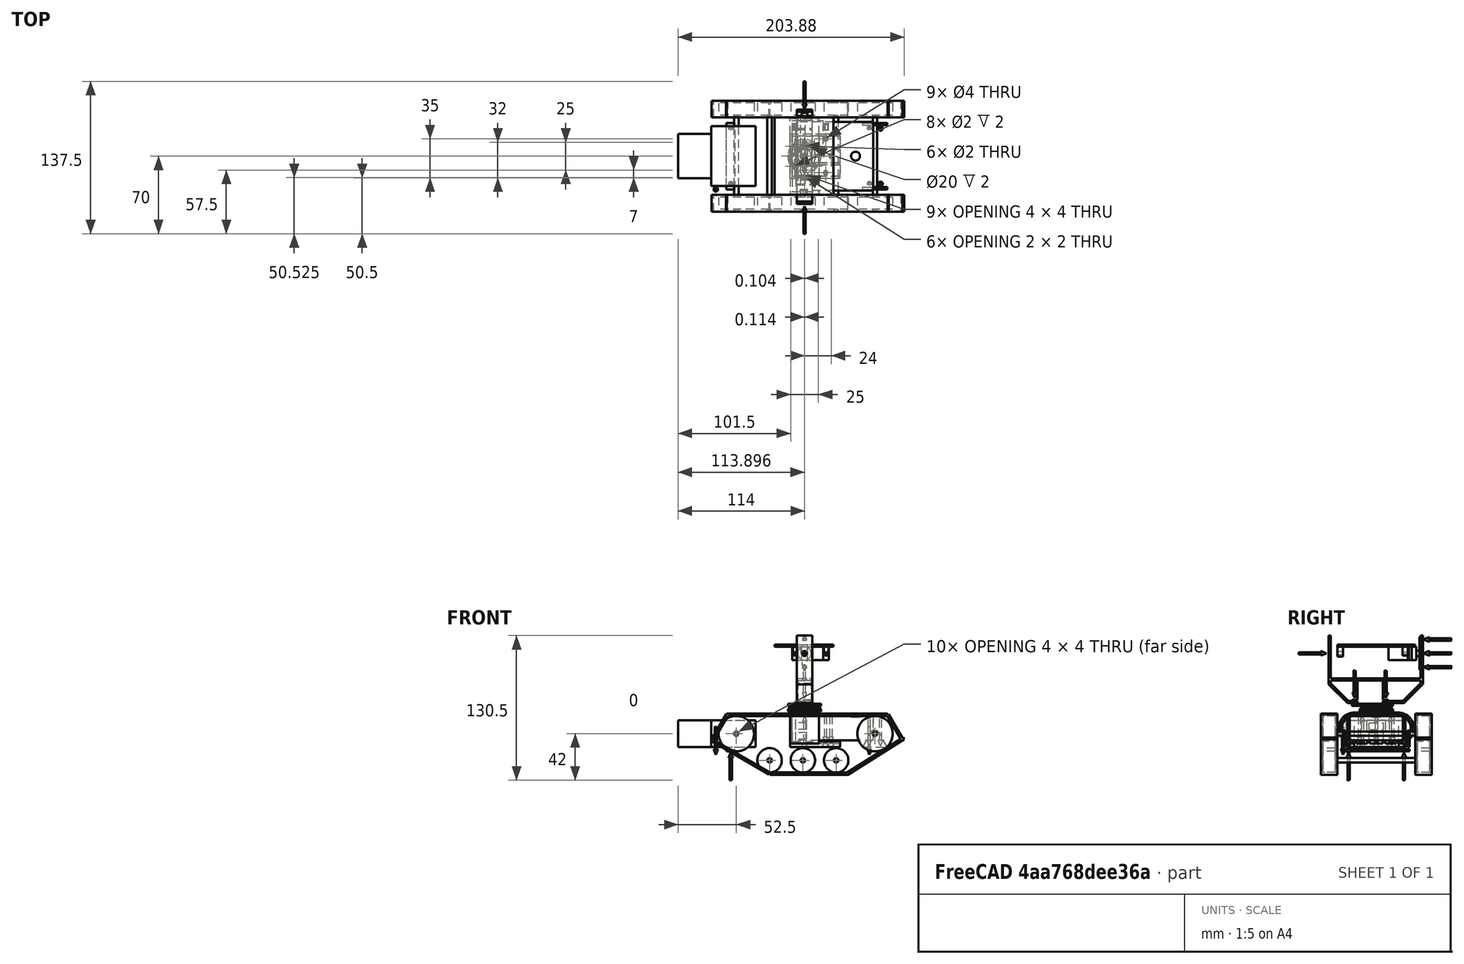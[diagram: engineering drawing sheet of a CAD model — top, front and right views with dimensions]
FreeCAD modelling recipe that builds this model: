
FCSTD DOCUMENT
Label: androidtank_9
License: CC-BY 3.0
LicenseURL: http://creativecommons.org/licenses/by/3.0/
objects: Part::Cylinder×57, Part::MultiFuse×45, Part::Box×39, Part::Cut×9, Part::Sphere×8, App::DocumentObjectGroup×2, Part::FeaturePython×1, Mesh::Feature×1, Part::Cone×1
note: 160 computed .brp shape members not serialized (recipe doc carries the construction recipe); baked Part::Feature solids carry a one-line shape summary decoded from their .brp

FEATURE [Part::Box] Box001001  label="Moter Unit2"
  Height = 24
  Length = 30
  Placement = pos=(-34,10,2) rot=(0,0,1;0rad)
  Width = 40
FEATURE [Part::Cylinder] Cylinder  label="Shaft"
  Angle = 360
  Height = 100
  Placement = pos=(20,-20,14) rot=(-1,0,0;1.5708rad)
  Radius = 2
FEATURE [Part::Box] Box001002
  Height = 2
  Length = 145
  Placement = pos=(10,-20,30) rot=(0,0,1;0rad)
  Width = 15
FEATURE [Part::Box] Box001002001
  Height = 2
  Length = 70
  Placement = pos=(49,-20,-23) rot=(0,0,1;0rad)
  Width = 15
FEATURE [Part::Box] Box001002001001
  Height = 2
  Length = 60
  Placement = pos=(119,-20,-23) rot=(0,-1,0;0.558505rad)
  Width = 15
FEATURE [Part::Box] Box001002001002
  Height = 2
  Length = 60
  Placement = pos=(49,-20,-21) rot=(0,1,0;3.66519rad)
  Width = 15
FEATURE [Part::Box] Box001002001003
  Height = 2
  Length = 26
  Placement = pos=(-2,-20,8) rot=(0,-1,0;1.0472rad)
  Width = 15
FEATURE [Part::Box] Box001002001003001
  Height = 2
  Length = 26
  Placement = pos=(169,-20,9) rot=(0,-1,0;2.0944rad)
  Width = 15
FEATURE [Part::MultiFuse] Fusion002001002  label="Caterpiller1"
  Shapes = -> [Box001002,Box001002001,Box001002001002,Box001002001001,Box001002001003,Box001002001003001]
FEATURE [Part::MultiFuse] Fusion002001002001  label="Caterpiller2"
  Placement = pos=(0,85,0) rot=(0,0,1;0rad)
  Shapes = -> [Box001002,Box001002001,Box001002001002,Box001002001001,Box001002001003,Box001002001003001]
FEATURE [Part::Cylinder] Cylinder002001001002  label="Wheel006"
  Angle = 360
  Height = 11
  Placement = pos=(20,78,14) rot=(1,0,0;1.5708rad)
  Radius = 11
FEATURE [Part::Cylinder] Cylinder002001001002001  label="Wheel007"
  Angle = 360
  Height = 11
  Placement = pos=(20,-7,14) rot=(1,0,0;1.5708rad)
  Radius = 11
FEATURE [Part::Cylinder] Cylinder002001002001  label="Shaft002"
  Angle = 360
  Height = 100
  Placement = pos=(20,-20,14) rot=(-1,0,0;1.5708rad)
  Radius = 2
FEATURE [Part::MultiFuse] Fusion002001002002002  label="SWheelSet1"
  Placement = pos=(28.5,0,-24) rot=(0,0,1;0rad)
  Shapes = -> [Cylinder002001002001,Cylinder002001001002,Cylinder002001001002001]
FEATURE [Part::MultiFuse] Fusion002001002002002001  label="SWheelSet2"
  Placement = pos=(58.5,0,-24) rot=(0,0,1;0rad)
  Shapes = -> [Cylinder002001002001,Cylinder002001001002,Cylinder002001001002001]
FEATURE [Part::MultiFuse] Fusion002001002002002001001  label="SWheelSet3"
  Placement = pos=(88.5,0,-24) rot=(0,0,1;0rad)
  Shapes = -> [Cylinder002001002001,Cylinder002001001002,Cylinder002001001002001]
FEATURE [Part::Box] Box001002001003002
  Height = 22
  Length = 70
  Placement = pos=(0,0,-11) rot=(0,0,1;0rad)
  Width = 40
FEATURE [Part::Cylinder] Cylinder002001001002002
  Angle = 360
  Height = 70
  Placement = pos=(0,0,0) rot=(0,1,0;1.5708rad)
  Radius = 11
FEATURE [Part::Cylinder] Cylinder001
  Angle = 360
  Height = 70
  Placement = pos=(0,40,0) rot=(0,1,0;1.5708rad)
  Radius = 11
FEATURE [Part::Cylinder] Cylinder002001001002003  label="PowerButton"
  Angle = 360
  Height = 2
  Placement = pos=(16,20,10) rot=(0,0,1;0rad)
  Radius = 4
FEATURE [Part::Box] Box001002001003003  label="USB1"
  Height = 6
  Length = 15
  Placement = pos=(60,13.5,-1) rot=(0,0,1;0rad)
  Width = 13
FEATURE [Part::Box] Box001001001  label="USB2"
  Height = 6
  Length = 15
  Placement = pos=(60,13.5,-10) rot=(0,0,1;0rad)
  Width = 13
FEATURE [Part::MultiFuse] Fusion002001002002002001002
  Shapes = -> [Cylinder001,Box001002001003002,Cylinder002001001002002]
FEATURE [Part::MultiFuse] Fusion001001
  Shapes = -> [Box001001001,Cylinder002001001002003,Box001002001003003]
FEATURE [Part::Cut] Cut  label="Eneloop"
  Base = -> Fusion002001002002002001002
  Placement = pos=(142,50,19) rot=(0,0,1;3.14159rad)
  Tool = -> Fusion001001
FEATURE [Part::Cylinder] Cylinder001001  label="Cylinder002"
  Angle = 360
  Height = 26
  Placement = pos=(0,50,19) rot=(0,1,0;1.5708rad)
  Radius = 14
FEATURE [Part::Box] Box001002001003002001  label="Box001002001003002001001001001006001001002001003001006001002"
  Height = 28
  Length = 26
  Placement = pos=(0,10,5) rot=(0,0,1;0rad)
  Width = 40
FEATURE [Part::Cylinder] Cylinder002001001002002001  label="Cylinder003"
  Angle = 360
  Height = 26
  Placement = pos=(0,10,19) rot=(0,1,0;1.5708rad)
  Radius = 14
FEATURE [Part::Box] Box001  label="Moter Unit1"
  Height = 24
  Length = 40
  Placement = pos=(-4,3,2) rot=(0,0,1;0rad)
  Width = 54
FEATURE [Part::Box] Box001002001003002001001  label="Box003"
  Height = 5
  Length = 45
  Placement = pos=(0,10,2) rot=(0,0,1;0rad)
  Width = 40
FEATURE [Part::Box] Box001002001003002001002  label="Box004"
  Height = 24
  Length = 26
  Placement = pos=(2,10,7) rot=(0,0,1;0rad)
  Width = 40
FEATURE [Part::Cylinder] Cylinder001001001  label="Cylinder004"
  Angle = 360
  Height = 26
  Placement = pos=(2,50,19) rot=(0,1,0;1.5708rad)
  Radius = 12
FEATURE [Part::Cylinder] Cylinder002001001002002001001  label="Cylinder005"
  Angle = 360
  Height = 26
  Placement = pos=(2,10,19) rot=(0,1,0;1.5708rad)
  Radius = 12
FEATURE [Part::Box] Box001002001003002001001001  label="Box006"
  Height = 3
  Length = 45
  Placement = pos=(2,12,5) rot=(0,0,1;0rad)
  Width = 10
FEATURE [Part::Box] Box001002001003002001001001001  label="Box007"
  Height = 3
  Length = 45
  Placement = pos=(2,24,5) rot=(0,0,1;0rad)
  Width = 12
FEATURE [Part::Box] Box001002001003002001001001001001  label="Box008"
  Height = 3
  Length = 45
  Placement = pos=(2,38,5) rot=(0,0,1;0rad)
  Width = 10
FEATURE [Part::MultiFuse] Fusion002001002002002001003
  Shapes = -> [Box001002001003002001,Cylinder001001,Cylinder002001001002002001,Box001002001003002001001]
FEATURE [Part::Cylinder] Cylinder002001001002002001002001  label="Cylinder007"
  Angle = 360
  Height = 40
  Placement = pos=(80,17.5,0) rot=(0,0,1;0rad)
  Radius = 1
FEATURE [Part::Cylinder] Cylinder002001001002002001002  label="Cylinder006"
  Angle = 360
  Height = 40
  Placement = pos=(80,42.5,0) rot=(0,0,1;0rad)
  Radius = 1
FEATURE [Part::Cylinder] Cylinder002001001002002001002001001  label="Cylinder008"
  Angle = 360
  Height = 40
  Placement = pos=(104,30,0) rot=(0,0,1;0rad)
  Radius = 2
FEATURE [Part::Cylinder] Cylinder002001001002002001002001002  label="Cylinder009"
  Angle = 360
  Height = 40
  Placement = pos=(99,45.5,0) rot=(0,0,1;0rad)
  Radius = 2
FEATURE [Part::Cylinder] Cylinder002001001002002001002001003  label="Cylinder0010"
  Angle = 360
  Height = 40
  Placement = pos=(99,15,0) rot=(0,0,1;0rad)
  Radius = 2
FEATURE [Part::Box] Box001002001003002001001001001006  label="Box009"
  Height = 2
  Length = 53
  Placement = pos=(47,-5,100) rot=(0,0,1;0rad)
  Width = 70
FEATURE [Part::Box] Box001002001003002001001001001006001  label="Box010"
  Height = 44
  Length = 14
  Placement = pos=(67,70,66) rot=(0,0,1;0rad)
  Width = 2
FEATURE [Part::Box] Box001002001003002001001001001006001001  label="Box011"
  Height = 2
  Length = 13
  Placement = pos=(67.5,12.5,48) rot=(0,0,1;0rad)
  Width = 23.5
FEATURE [Part::Box] Box001002001003002001001001001006001001001  label="Box012"
  Height = 44
  Length = 14
  Placement = pos=(67,-13,66) rot=(0,0,1;0rad)
  Width = 2
FEATURE [Part::Cylinder] Cylinder002001001002002001002001008  label="Hole1"
  Angle = 360
  Height = 20
  Placement = pos=(74,-20,94) rot=(-1,0,0;1.5708rad)
  Radius = 1.5
FEATURE [Part::Cylinder] Cylinder002001001002002001002001008001  label="Hole2"
  Angle = 360
  Height = 20
  Placement = pos=(74,60,106.5) rot=(-1,0,0;1.5708rad)
  Radius = 1
FEATURE [Part::Cylinder] Cylinder002001001002002001002001008001001  label="Hole4"
  Angle = 360
  Height = 20
  Placement = pos=(74,38.5,41) rot=(0,0,1;0rad)
  Radius = 1
FEATURE [Part::Cylinder] Cylinder002001001002002001002001008001001001  label="Hole3"
  Angle = 360
  Height = 20
  Placement = pos=(74,60,81.5) rot=(-1,0,0;1.5708rad)
  Radius = 1
FEATURE [Part::Cylinder] Cylinder002001001002002001002001008001001002  label="Hole5"
  Angle = 360
  Height = 20
  Placement = pos=(74,10.5,41) rot=(0,0,1;0rad)
  Radius = 1
FEATURE [Part::Box] Box001002001003002001001001001006001001001001  label="Box013"
  Height = 24
  Length = 14
  Placement = pos=(67,4,49) rot=(1,0,0;0.785397rad)
  Width = 2
FEATURE [Part::Box] Box001002001003002001001001001006001001001001001  label="Box014"
  Height = 24
  Length = 14
  Placement = pos=(67,53.41,50.41) rot=(-1,0,0;0.785397rad)
  Width = 2
FEATURE [Part::Box] Box001002001003002001001001001006001001002001  label="Box016"
  Height = 2
  Length = 14
  Placement = pos=(67,4,49) rot=(0,0,1;0rad)
  Width = 9
FEATURE [Part::Box] Box001002001003002001001001001006001001002001001  label="Box017"
  Height = 2
  Length = 14
  Placement = pos=(67,36,49) rot=(0,0,1;0rad)
  Width = 19
FEATURE [Part::Box] Box001002001003002001001001001006001001002001002  label="Box015"
  Height = 2
  Length = 14
  Placement = pos=(67,-13,69.5) rot=(0,0,1;0rad)
  Width = 85
FEATURE [Part::MultiFuse] Fusion002001002002002001009
  Shapes = -> [Box001002001003002001001001001006001,Box001002001003002001001001001006001001001001,Box001002001003002001001001001006001001001,Box001002001003002001001001001006001001001001001,Box001002001003002001001001001006001001002001,Box001002001003002001001001001006001001002001002,Box001002001003002001001001001006001001002001001]
FEATURE [Part::Cylinder] Cylinder002001001002002001002001008001001002001  label="Hole006"
  Angle = 360
  Height = 20
  Placement = pos=(74,10.5,60) rot=(0,0,1;0rad)
  Radius = 2
FEATURE [Part::Cylinder] Cylinder002001001002002001002001008001001002002  label="Hole007"
  Angle = 360
  Height = 20
  Placement = pos=(74,38.5,60) rot=(0,0,1;0rad)
  Radius = 2
FEATURE [Part::MultiFuse] Fusion002001002002002001010
  Shapes = -> [Cylinder002001001002002001002001008001,Box001002001003002001001001001006001001,Cylinder002001001002002001002001008001001,Cylinder002001001002002001002001008,Cylinder002001001002002001002001008001001001,Cylinder002001001002002001002001008001001002,Cylinder002001001002002001002001008001001002002,Cylinder002001001002002001002001008001001002001]
FEATURE [Part::Cut] Cut003  label="HeadFrame"
  Base = -> Fusion002001002002002001009
  Placement = pos=(6,0,-7.5) rot=(0,0,1;0rad)
  Tool = -> Fusion002001002002002001010
FEATURE [Part::Cylinder] Cylinder002001001002002001002001008001001002003  label="Cylinder025"
  Angle = 360
  Height = 5
  Placement = pos=(74,0,94) rot=(1,0,0;1.5708rad)
  Radius = 3
FEATURE [Part::Box] Box001002001003002001001001001006001001002001003  label="Box020"
  Height = 6
  Length = 6
  Placement = pos=(71,-5,94) rot=(0,0,1;0rad)
  Width = 5
FEATURE [Part::Cylinder] Cylinder002001001002002001002001008001001002003001  label="Cylinder026"
  Angle = 360
  Height = 7
  Placement = pos=(74,1,94) rot=(1,0,0;1.5708rad)
  Radius = 1.5
FEATURE [Part::Box] Box001002001003002001001001001006001001002001003001001  label="Box022"
  Height = 6
  Length = 4
  Placement = pos=(91.5,53.5,94) rot=(0,0,1;0rad)
  Width = 5
FEATURE [Part::Cylinder] Cylinder002001001002002001002001008001001002003002  label="Cylinder027"
  Angle = 360
  Height = 5
  Placement = pos=(65.5,58.5,94) rot=(1,0,0;1.5708rad)
  Radius = 2
FEATURE [Part::Cylinder] Cylinder002001001002002001002001008001001002003002001  label="Cylinder028"
  Angle = 360
  Height = 5
  Placement = pos=(93.5,58.5,94) rot=(1,0,0;1.5708rad)
  Radius = 2
FEATURE [Part::Box] Box001002001003002001001001001006001001002001003001  label="Box021"
  Height = 6
  Length = 4
  Placement = pos=(63.5,53.5,94) rot=(0,0,1;0rad)
  Width = 5
FEATURE [Part::Cylinder] Cylinder002001001002002001002001008001001002003002002  label="Cylinder029"
  Angle = 360
  Height = 6
  Placement = pos=(65.5,59,94) rot=(1,0,0;1.5708rad)
  Radius = 1
FEATURE [Part::Cylinder] Cylinder002001001002002001002001008001001002003002001001  label="Cylinder030"
  Angle = 360
  Height = 6
  Placement = pos=(93.5,59,94) rot=(1,0,0;1.5708rad)
  Radius = 1
FEATURE [Part::MultiFuse] Fusion002001002002002001011
  Shapes = -> [Box001002001003002001001001001006,Box001002001003002001001001001006001001002001003001001,Cylinder002001001002002001002001008001001002003002001,Box001002001003002001001001001006001001002001003,Cylinder002001001002002001002001008001001002003,Box001002001003002001001001001006001001002001003001,Cylinder002001001002002001002001008001001002003002]
FEATURE [Part::MultiFuse] Fusion002001002002002001012
  Shapes = -> [Cylinder002001001002002001002001008001001002003001,Cylinder002001001002002001002001008001001002003002002,Cylinder002001001002002001002001008001001002003002001001]
FEATURE [Part::Cut] Cut002003  label="HeadMount"
  Base = -> Fusion002001002002002001011
  Placement = pos=(6,0,-7.5) rot=(0,0,1;0rad)
  Tool = -> Fusion002001002002002001012
FEATURE [Part::Cylinder] Cylinder002001001002002001002001001001  label="Cylinder040"
  Angle = 360
  Height = 40
  Placement = pos=(80,30,0) rot=(0,0,1;0rad)
  Radius = 2
FEATURE [Part::Box] Box001002001003002001001001001006001001002001003001002  label="ServoBody"
  Height = 21
  Length = 23
  Width = 12
FEATURE [Part::Cylinder] Cylinder002001001002002001002001008001001002003002001002  label="ServoBody2"
  Angle = 360
  Height = 4
  Placement = pos=(6,6,21) rot=(0,0,1;0rad)
  Radius = 6
FEATURE [Part::Box] Box001002001003002001001001001006001001002001003001003  label="ServoBody3"
  Height = 1
  Length = 33
  Placement = pos=(-5,0,17.5) rot=(0,0,1;0rad)
  Width = 12
FEATURE [Part::Cylinder] Cylinder001001002  label="ServoAxis"
  Angle = 360
  Height = 4
  Placement = pos=(6,6,24) rot=(0,0,1;0rad)
  Radius = 2.5
FEATURE [Part::MultiFuse] Fusion005  label="ServoArmL"
  Shapes = -> [Cylinder001001002,Box001002001003002001001001001006001001002001003001003,Box001002001003002001001001001006001001002001003001002,Cylinder002001001002002001002001008001001002003002001002]
FEATURE [Part::MultiFuse] Fusion006  label="ServoYaw"
  Placement = pos=(86,36,62) rot=(0.707107,-0.707107,0;3.14159rad)
  Shapes = -> [Fusion005]
FEATURE [Part::Cylinder] Cylinder003001001004  label="Cylinder002001001002002001002001008001001002003002001006"
  Angle = 360
  Height = 0.5
  Placement = pos=(-2.5,6,20.5) rot=(0,0,1;0rad)
  Radius = 2
FEATURE [Part::Cylinder] Cylinder003001001005  label="Cylinder011"
  Angle = 360
  Height = 2
  Placement = pos=(6,6,21) rot=(0,0,1;0rad)
  Radius = 15
FEATURE [Part::Cylinder] Cylinder003001001004001  label="Cylinder010"
  Angle = 360
  Height = 0.5
  Placement = pos=(25.5,6,20.5) rot=(0,0,1;0rad)
  Radius = 2
FEATURE [Part::Cylinder] Cylinder003001001005001  label="Cylinder012"
  Angle = 360
  Height = 2
  Placement = pos=(6,6,21) rot=(0,0,1;0rad)
  Radius = 6.5
FEATURE [Part::Cylinder] Cylinder003001001005001001  label="Cylinder013"
  Angle = 360
  Height = 2
  Placement = pos=(12,6,21) rot=(0,0,1;0rad)
  Radius = 3.5
FEATURE [Part::Box] Box002
  Height = 2
  Length = 10
  Placement = pos=(18,3,21) rot=(0,0,1;0rad)
  Width = 6
FEATURE [Part::Cylinder] Cylinder003001001004002  label="Cylinder014"
  Angle = 360
  Height = 5
  Placement = pos=(-2.5,6,19.5) rot=(0,0,1;0rad)
  Radius = 1
FEATURE [Part::Cylinder] Cylinder003001001004001001  label="Cylinder015"
  Angle = 360
  Height = 5
  Placement = pos=(25.5,6,19.5) rot=(0,0,1;0rad)
  Radius = 1
FEATURE [Part::MultiFuse] Fusion008
  Shapes = -> [Cylinder003001001005,Box002,Cylinder003001001004,Cylinder003001001004001]
FEATURE [Part::MultiFuse] Fusion009
  Shapes = -> [Cylinder003001001005001,Cylinder003001001005001001,Cylinder003001001004002,Cylinder003001001004001001]
FEATURE [Part::Cut] Cut002  label="Guide1"
  Base = -> Fusion008
  Placement = pos=(86,36,62) rot=(-0.705662,0.708549,0;3.14159rad)
  Tool = -> Fusion009
FEATURE [Part::Box] Box001002001003002001001001001006001001002001003001004  label="ServoBody004"
  Height = 21
  Length = 23
  Width = 12
FEATURE [Part::Cylinder] Cylinder002001001002002001002001008001001002003002001003  label="ServoBody005"
  Angle = 360
  Height = 4
  Placement = pos=(6,6,21) rot=(0,0,1;0rad)
  Radius = 6
FEATURE [Part::Box] Box001002001003002001001001001006001001002001003001005  label="ServoBody006"
  Height = 1
  Length = 33
  Placement = pos=(-5,0,17.5) rot=(0,0,1;0rad)
  Width = 12
FEATURE [Part::Cylinder] Cylinder001001003  label="ServoAxis001"
  Angle = 360
  Height = 4
  Placement = pos=(6,6,24) rot=(0,0,1;0rad)
  Radius = 2.5
FEATURE [Part::MultiFuse] Fusion005001  label="ServoArmL001"
  Shapes = -> [Cylinder001001003,Box001002001003002001001001001006001001002001003001005,Box001002001003002001001001001006001001002001003001004,Cylinder002001001002002001002001008001001002003002001003]
FEATURE [Part::Cylinder] Cylinder002001001002002001002001008001001002003002001004  label="Cylinder002001001002002001002001008001001002003002001012"
  Angle = 360
  Height = 2
  Radius = 2.5
FEATURE [Part::FeaturePython] Scale  # Draft clone (typed FeaturePython)
  Objects = -> [Cylinder002001001002002001002001008001001002003002001004]
  Placement = pos=(0,0,1) rot=(0,0,1;0rad)
  Scale = (6,1,0.5)
FEATURE [Part::MultiFuse] Fusion  label="Arm"
  Placement = pos=(6,6,27) rot=(0,0,1;1.5708rad)
  Shapes = -> [Cylinder002001001002002001002001008001001002003002001004,Scale]
FEATURE [Part::MultiFuse] Fusion006001  label="ServoPitch"
  Placement = pos=(74,41,92.5) rot=(-1,0,0;1.5708rad)
  Shapes = -> [Fusion005001,Fusion]
FEATURE [Part::Cylinder] Cylinder002001001002002001002001008001001002003002001005  label="Wheel1"
  Angle = 360
  Height = 11
  Placement = pos=(20,78,14) rot=(1,0,0;1.5708rad)
  Radius = 16
FEATURE [Part::Cylinder] Cylinder002001001002002001002001008001001002003002001005001  label="Wheel2"
  Angle = 360
  Height = 11
  Placement = pos=(20,-7,14) rot=(1,0,0;1.5708rad)
  Radius = 16
FEATURE [Part::MultiFuse] Fusion002001002002002001014  label="LWheelSet1"
  Placement = pos=(-1.5,0,0) rot=(0,0,1;0rad)
  Shapes = -> [Cylinder,Cylinder002001001002002001002001008001001002003002001005,Cylinder002001001002002001002001008001001002003002001005001]
FEATURE [Part::MultiFuse] Fusion002001002002002001014001  label="LWheelSet2"
  Placement = pos=(123.5,0,0) rot=(0,0,1;0rad)
  Shapes = -> [Cylinder,Cylinder002001001002002001002001008001001002003002001005,Cylinder002001001002002001002001008001001002003002001005001]
FEATURE [Part::Cylinder] Cylinder003001001003  label="Cylinder002001001002002001002001008001001002003002001013"
  Angle = 360
  Height = 2
  Placement = pos=(6,6,26) rot=(0,0,1;0rad)
  Radius = 15
FEATURE [Part::Sphere] Sphere
  Angle1 = -90
  Angle2 = 0
  Angle3 = 360
  Placement = pos=(-3,-3,26) rot=(0,0,1;0rad)
  Radius = 2
FEATURE [Part::Sphere] Sphere001
  Angle1 = -90
  Angle2 = 0
  Angle3 = 360
  Placement = pos=(15,-3,26) rot=(0,0,1;0rad)
  Radius = 2
FEATURE [Part::Sphere] Sphere001001  label="Sphere002"
  Angle1 = -90
  Angle2 = 0
  Angle3 = 360
  Placement = pos=(15,15,26) rot=(0,0,1;0rad)
  Radius = 2
FEATURE [Part::Sphere] Sphere001001001  label="Sphere003"
  Angle1 = -90
  Angle2 = 0
  Angle3 = 360
  Placement = pos=(-3,15,26) rot=(0,0,1;0rad)
  Radius = 2
FEATURE [Part::Cylinder] Cylinder003001001005001004  label="Cylinder020"
  Angle = 360
  Height = 4
  Placement = pos=(-6.5,6,26) rot=(0,0,1;0rad)
  Radius = 1
FEATURE [Part::Cylinder] Cylinder003001001001003  label="Cylinder021"
  Angle = 360
  Height = 4
  Placement = pos=(18.5,6,26) rot=(0,0,1;0rad)
  Radius = 1
FEATURE [Part::Cylinder] Cylinder003001001005001003001  label="Cylinder022"
  Angle = 360
  Height = 5
  Placement = pos=(-3,-3,26) rot=(0,0,1;0rad)
  Radius = 1
FEATURE [Part::Cylinder] Cylinder003001001001002001  label="Cylinder023"
  Angle = 360
  Height = 5
  Placement = pos=(15,-3,26) rot=(0,0,1;0rad)
  Radius = 1
FEATURE [Part::Sphere] Sphere001001001001  label="Sphere004"
  Angle1 = -90
  Angle2 = 0
  Angle3 = 360
  Placement = pos=(-6.5,6,26) rot=(0,0,1;0rad)
  Radius = 2
FEATURE [Part::Sphere] Sphere001001001001001  label="Sphere005"
  Angle1 = -90
  Angle2 = 0
  Angle3 = 360
  Placement = pos=(18.5,6,26) rot=(0,0,1;0rad)
  Radius = 2
FEATURE [Part::Sphere] Sphere001001001001001001  label="Sphere006"
  Angle1 = -90
  Angle2 = 0
  Angle3 = 360
  Placement = pos=(6,-6.5,26) rot=(0,0,1;0rad)
  Radius = 2
FEATURE [Part::Sphere] Sphere001001001001001001001  label="Sphere007"
  Angle1 = -90
  Angle2 = 0
  Angle3 = 360
  Placement = pos=(6,18.5,26) rot=(0,0,1;0rad)
  Radius = 2
FEATURE [Part::Cylinder] Cylinder003001001003001  label="Cylinder024"
  Angle = 360
  Height = 2
  Placement = pos=(6,6,26) rot=(0,0,1;0rad)
  Radius = 10
FEATURE [Part::MultiFuse] Fusion014
  Shapes = -> [Sphere,Cylinder003001001003,Sphere001001001,Sphere001001001001001001,Sphere001001001001,Sphere001,Sphere001001,Sphere001001001001001001001,Sphere001001001001001]
FEATURE [Part::Cylinder] Cylinder003001001005001003001001  label="Cylinder002001001002002001002001008001001002003002001014"
  Angle = 360
  Height = 5
  Placement = pos=(-3,15,26) rot=(0,0,1;0rad)
  Radius = 1
FEATURE [Part::Cylinder] Cylinder003001001001002001001  label="Cylinder002001001002002001002001008001001002003002001015"
  Angle = 360
  Height = 5
  Placement = pos=(15,15,26) rot=(0,0,1;0rad)
  Radius = 1
FEATURE [Part::Cylinder] Cylinder003001001005001003001001001  label="Cylinder002001001002002001002001008001001002003002001016"
  Angle = 360
  Height = 5
  Placement = pos=(6,18.5,26) rot=(0,0,1;0rad)
  Radius = 1
FEATURE [Part::Cylinder] Cylinder003001001005001003001001001001  label="Cylinder002001001002002001002001008001001002003002001017"
  Angle = 360
  Height = 5
  Placement = pos=(6,-6.5,26) rot=(0,0,1;0rad)
  Radius = 1
FEATURE [Part::MultiFuse] Fusion015
  Shapes = -> [Cylinder003001001003001,Cylinder003001001005001004,Cylinder003001001001003,Cylinder003001001005001003001,Cylinder003001001001002001,Cylinder003001001005001003001001,Cylinder003001001005001003001001001001,Cylinder003001001001002001001,Cylinder003001001005001003001001001]
FEATURE [Part::Cut] Cut002005  label="Guide2"
  Base = -> Fusion014
  Placement = pos=(74,36,62) rot=(1,0,0;3.14159rad)
  Tool = -> Fusion015
FEATURE [Part::MultiFuse] Fusion002001002002002001014002
  Shapes = -> [Box001002001003002001002,Cylinder001001001,Cylinder002001001002002001001,Box001002001003002001001001,Box001002001003002001001001001,Box001002001003002001001001001001]
FEATURE [Part::Cut] Cut002006
  Base = -> Fusion002001002002002001003
  Placement = pos=(67,0,0) rot=(0,0,1;0rad)
  Tool = -> Fusion002001002002002001014002
FEATURE [Part::Cylinder] Cylinder002001001002002001002001001001001  label="Cylinder041"
  Angle = 360
  Height = 20
  Placement = pos=(80,42.5,0) rot=(0,0,1;0rad)
  Radius = 2
FEATURE [Part::Cylinder] Cylinder002001001002002001002001001001001001  label="Cylinder042"
  Angle = 360
  Height = 20
  Placement = pos=(80,17.5,0) rot=(0,0,1;0rad)
  Radius = 2
FEATURE [Part::Box] Box001002001003003001  label="USB003"
  Height = 10
  Length = 15
  Placement = pos=(60,21.5,16) rot=(0,0,1;0rad)
  Width = 17
FEATURE [Part::MultiFuse] Fusion002001002002002001014003
  Shapes = -> [Cylinder002001001002002001002001,Cylinder002001001002002001002,Cylinder002001001002002001002001001,Cylinder002001001002002001002001002,Cylinder002001001002002001002001003,Cylinder002001001002002001002001001001,Cylinder002001001002002001002001001001001,Box001002001003003001,Cylinder002001001002002001002001001001001001]
FEATURE [Part::Cut] Cut002007  label="BatteryFrame2"
  Base = -> Cut002006
  Tool = -> Fusion002001002002002001014003
FEATURE [Part::Box] Box001002001003002001001001001006001001002001003001006  label="Box040"
  Height = 15
  Length = 22
  Placement = pos=(0,0,2) rot=(0,0,1;0rad)
  Width = 2
FEATURE [Part::Box] Box001002001003002001001001001006001001002001003001006001  label="Box041"
  Height = 20
  Length = 10
  Placement = pos=(22,0,2) rot=(0,-1,0;0.523599rad)
  Width = 2
FEATURE [Part::Box] Box001002001003002001001001001006001001002001003001006001001  label="Box042"
  Height = 20
  Length = 10
  Placement = pos=(-8.71,0,7) rot=(0,1,0;0.523599rad)
  Width = 2
FEATURE [Part::MultiFuse] Fusion002001002002002001014004
  Shapes = -> [Box001002001003002001001001001006001001002001003001006001001,Box001002001003002001001001001006001001002001003001006001]
FEATURE [Part::Cut] Cut002008  label="LWheelMount1"
  Base = -> Box001002001003002001001001001006001001002001003001006
  Placement = pos=(132.5,0,0) rot=(0,0,1;0rad)
  Tool = -> Fusion002001002002002001014004
FEATURE [Part::Cut] Cut002008001  label="LWheelMount2"
  Base = -> Box001002001003002001001001001006001001002001003001006
  Placement = pos=(132.5,58,0) rot=(0,0,1;0rad)
  Tool = -> Fusion002001002002002001014004
FEATURE [Mesh::Feature] UniversalPlate
FEATURE [Part::Box] Box  label="MotorMount"
  Height = 2
  Length = 8
  Placement = pos=(9.5,0,-2) rot=(0,0,1;0rad)
  Width = 60
FEATURE [App::DocumentObjectGroup] ____________  label="DriveFrame"
  Group = -> [Box001,Box001001,Fusion002001002,Fusion002001002001,Fusion002001002002002,Fusion002001002002002001,Fusion002001002002002001001,Fusion002001002002002001014,Fusion002001002002002001014001,Cut002008,Cut002008001,UniversalPlate,Box]
FEATURE [Part::Cone] Cone
  Angle = 360
  Height = 5
  Placement = pos=(0,0,-5) rot=(0,0,1;0rad)
  Radius1 = 0
  Radius2 = 2
FEATURE [Part::Cylinder] Cylinder002001001002002001002001008001001002003002001005002
  Angle = 360
  Height = 20
  Radius = 1
FEATURE [Part::MultiFuse] Fusion002001002002002001014005  label="ArrowOrig"
  Shapes = -> [Cone,Cylinder002001001002002001002001008001001002003002001005002]
FEATURE [Part::MultiFuse] Fusion002001002002002001014005001  label="Arrow001"
  Placement = pos=(148.5,5,8) rot=(0,0,1;0rad)
  Shapes = -> [Cone,Cylinder002001001002002001002001008001001002003002001005002]
FEATURE [Part::MultiFuse] Fusion002001002002002001014005001001  label="Arrow002"
  Placement = pos=(138.5,5,0) rot=(0,0,1;0rad)
  Shapes = -> [Cone,Cylinder002001001002002001002001008001001002003002001005002]
FEATURE [Part::MultiFuse] Fusion002001002002002001014005001002  label="Arrow003"
  Placement = pos=(148.5,55,8) rot=(0,0,1;0rad)
  Shapes = -> [Cone,Cylinder002001001002002001002001008001001002003002001005002]
FEATURE [Part::MultiFuse] Fusion002001002002002001014005001002001  label="Arrow004"
  Placement = pos=(138.5,55,8) rot=(0,0,1;0rad)
  Shapes = -> [Cone,Cylinder002001001002002001002001008001001002003002001005002]
FEATURE [Part::MultiFuse] Fusion002001002002002001014005001002002  label="Arrow005"
  Placement = pos=(13.5,5,-8) rot=(1,0,0;3.14159rad)
  Shapes = -> [Cone,Cylinder002001001002002001002001008001001002003002001005002]
FEATURE [Part::MultiFuse] Fusion002001002002002001014005001002002001  label="Arrow006"
  Placement = pos=(13.5,55,-8) rot=(1,0,0;3.14159rad)
  Shapes = -> [Cone,Cylinder002001001002002001002001008001001002003002001005002]
FEATURE [Part::MultiFuse] Fusion002001002002002001014005001002002002  label="Arrow007"
  Placement = pos=(80,17.5,25) rot=(1,0,0;3.14159rad)
  Shapes = -> [Cone,Cylinder002001001002002001002001008001001002003002001005002]
FEATURE [Part::MultiFuse] Fusion002001002002002001014005001002002002001  label="Arrow008"
  Placement = pos=(80,42.5,25) rot=(1,0,0;3.14159rad)
  Shapes = -> [Cone,Cylinder002001001002002001002001008001001002003002001005002]
FEATURE [Part::MultiFuse] Fusion002001002002002001014005001002002002002  label="Arrow009"
  Placement = pos=(80,10.5,51) rot=(0,0,1;0rad)
  Shapes = -> [Cone,Cylinder002001001002002001002001008001001002003002001005002]
FEATURE [Part::MultiFuse] Fusion002001002002002001014005001002002002003  label="Arrow010"
  Placement = pos=(80,38.5,51) rot=(0,0,1;0rad)
  Shapes = -> [Cone,Cylinder002001001002002001002001008001001002003002001005002]
FEATURE [Part::MultiFuse] Fusion002001002002002001014005001002002002002001  label="Arrow011"
  Placement = pos=(80,77.5,86.5) rot=(-1,0,0;1.5708rad)
  Shapes = -> [Cone,Cylinder002001001002002001002001008001001002003002001005002]
FEATURE [Part::MultiFuse] Fusion002001002002002001014005001002002002002001001  label="Arrow012"
  Placement = pos=(80,77.5,99) rot=(-1,0,0;1.5708rad)
  Shapes = -> [Cone,Cylinder002001001002002001002001008001001002003002001005002]
FEATURE [Part::MultiFuse] Fusion002001002002002001014005001002002002002001001001  label="Arrow013"
  Placement = pos=(80,77.5,74) rot=(-1,0,0;1.5708rad)
  Shapes = -> [Cone,Cylinder002001001002002001002001008001001002003002001005002]
FEATURE [Part::MultiFuse] Fusion002001002002002001014005001002002002002001001002  label="Arrow014"
  Placement = pos=(80,-20,86.5) rot=(1,0,0;1.5708rad)
  Shapes = -> [Cone,Cylinder002001001002002001002001008001001002003002001005002]
FEATURE [Part::MultiFuse] Fusion002001002002002001014005001002002002002001001003  label="Arrow015"
  Placement = pos=(80,30,25) rot=(1,0,0;3.14159rad)
  Shapes = -> [Cone,Cylinder002001001002002001002001008001001002003002001005002]
FEATURE [Part::MultiFuse] Fusion002001002002002001014005001002002002002001001004  label="Arrow016"
  Placement = pos=(104,30,11) rot=(0,0,1;0rad)
  Shapes = -> [Cone,Cylinder002001001002002001002001008001001002003002001005002]
FEATURE [Part::MultiFuse] Fusion002001002002002001014005001002002002002001001004001  label="Arrow017"
  Placement = pos=(99,45,11) rot=(0,0,1;0rad)
  Shapes = -> [Cone,Cylinder002001001002002001002001008001001002003002001005002]
FEATURE [Part::MultiFuse] Fusion002001002002002001014005001002002002002001001004001001  label="Arrow018"
  Placement = pos=(99,15,11) rot=(0,0,1;0rad)
  Shapes = -> [Cone,Cylinder002001001002002001002001008001001002003002001005002]
FEATURE [App::DocumentObjectGroup] ____________001  label="Arrows"
  Group = -> [Fusion002001002002002001014005,Fusion002001002002002001014005001,Fusion002001002002002001014005001001,Fusion002001002002002001014005001002,Fusion002001002002002001014005001002001,Fusion002001002002002001014005001002002,Fusion002001002002002001014005001002002001,Fusion002001002002002001014005001002002002,Fusion002001002002002001014005001002002002001,Fusion002001002002002001014005001002002002002,+9 more]
